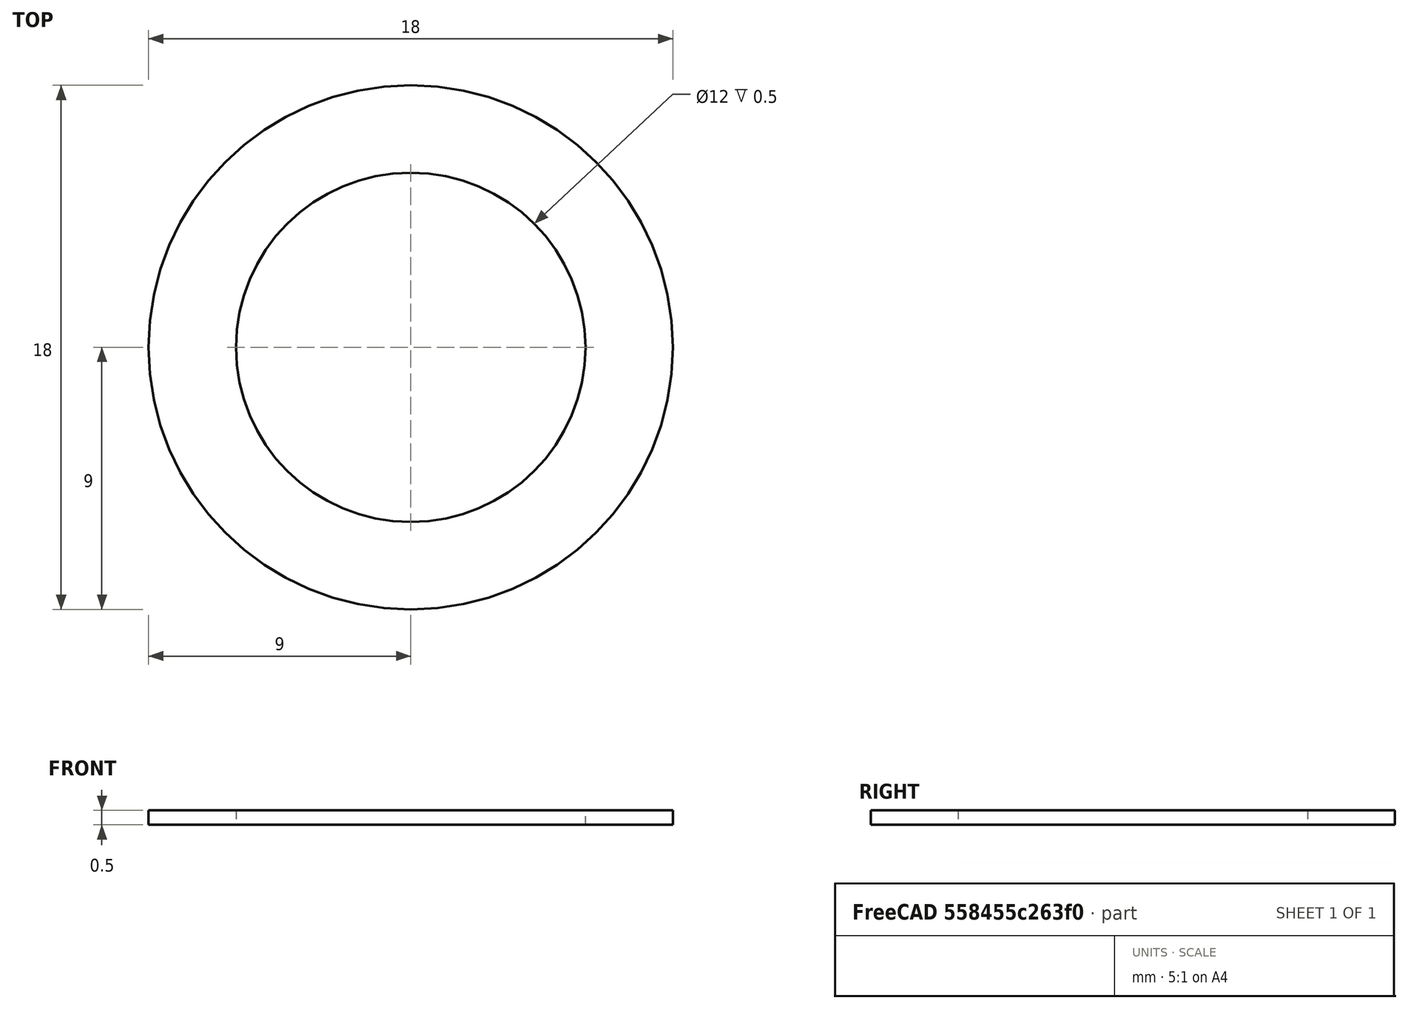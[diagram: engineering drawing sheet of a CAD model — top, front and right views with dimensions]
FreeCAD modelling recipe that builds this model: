
FCSTD DOCUMENT  (FreeCAD 0.19R24366 (Git))
Label: 12 x 18 x 0_5mm shim washer
License: All rights reserved
LicenseURL: http://en.wikipedia.org/wiki/All_rights_reserved
objects: Sketcher::SketchObject×1, PartDesign::Pad×1, PartDesign::Body×1
note: 4 computed .brp shape members not serialized (recipe doc carries the construction recipe); baked Part::Feature solids carry a one-line shape summary decoded from their .brp

FEATURE [Sketcher::SketchObject] Sketch
  FullyConstrained = true
  MapMode = 5
  Support = -> [XY_Plane]
  sketch-geometry (2):
    g0: Circle CenterX=0 CenterY=0 CenterZ=0 NormalX=0 NormalY=0 NormalZ=1 AngleXU=0 Radius=6
    g1: Circle CenterX=0 CenterY=0 CenterZ=0 NormalX=0 NormalY=0 NormalZ=1 AngleXU=0 Radius=9
  constraints (4):
    c: Coincident(g0,g-1)
    c: Coincident(g1,g0)
    c: Diameter(g0) = 12
    c: Diameter(g1) = 18
FEATURE [PartDesign::Pad] Pad
  Direction = (1,1,1)
  Length = 0.5
  Length2 = 100
  Profile = -> Sketch
  Type = 0
FEATURE [PartDesign::Body] Body
  Group = -> [Sketch,Pad]
  Origin = -> Origin
  Tip = -> Pad
